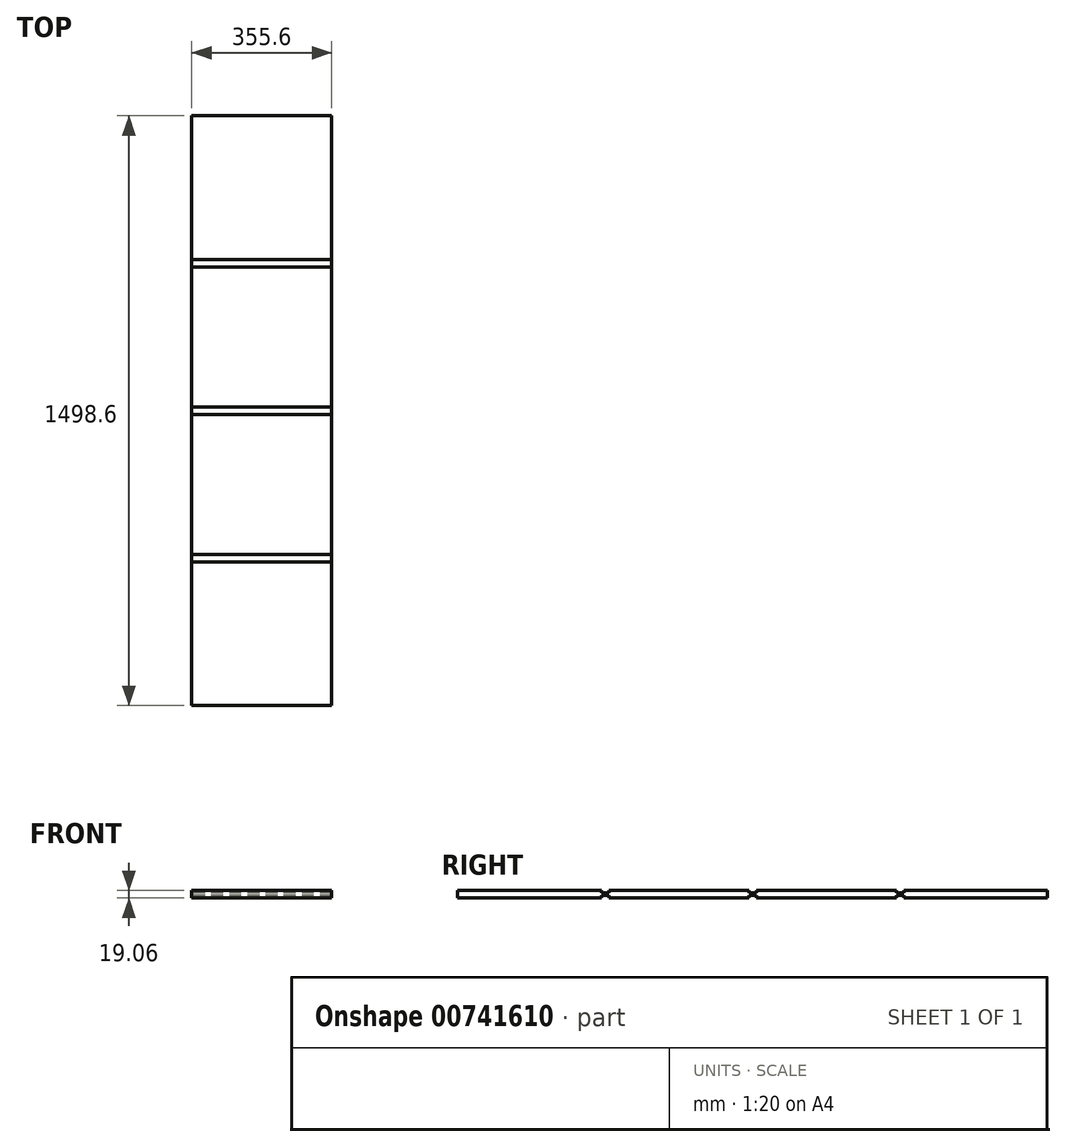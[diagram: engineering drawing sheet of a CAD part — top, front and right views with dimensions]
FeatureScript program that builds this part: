
annotation { "Feature Type Name" : "Feature", "Feature Type Description" : "" }
export const myFeature = defineFeature(function(context is Context, id is Id, definition is map)
    precondition{}
    {
        {
            var Q0;
            Q0=qCreatedBy(makeId("Right.planeOp"),FACE);
            var sketch = newSketch(context, id + "F0", { "sketchPlane" : qUnion([Q0])});
            skLineSegment(sketch, "E0.bottom", {"start": v(749.3, 9.53) * mm, "end": v(384.17, 9.53) * mm});
            skLineSegment(sketch, "E0.top", {"start": v(749.3, -9.53) * mm, "end": v(384.17, -9.53) * mm});
            skLineSegment(sketch, "E0.left", {"start": v(749.3, 9.52) * mm, "end": v(749.3, -9.52) * mm});
            skLineSegment(sketch, "E0.right", {"start": v(-749.3, 9.53) * mm, "end": v(-749.3, -9.53) * mm});
            skPoint(sketch, "E0.middle", {"position": v(0, 0) * mm});
            skLineSegment(sketch, "E1", {"start": v(-749.3, 9.53) * mm, "end": v(-384.17, 9.53) * mm});
            skLineSegment(sketch, "E2.top", {"start": v(-384.17, 3.18) * mm, "end": v(-365.12, 3.18) * mm});
            skLineSegment(sketch, "E2.left", {"start": v(-384.17, 9.53) * mm, "end": v(-384.17, 3.18) * mm});
            skLineSegment(sketch, "E2.right", {"start": v(-365.12, 9.53) * mm, "end": v(-365.12, 3.18) * mm});
            skLineSegment(sketch, "E3", {"start": v(-365.12, 9.53) * mm, "end": v(-9.52, 9.53) * mm});
            skLineSegment(sketch, "E4.top", {"start": v(-9.52, 3.18) * mm, "end": v(0, 3.18) * mm});
            skLineSegment(sketch, "E4.left", {"start": v(-9.52, 9.53) * mm, "end": v(-9.52, 3.18) * mm});
            skLineSegment(sketch, "E5.MirrorCS", {"start": v(9.52, 3.18) * mm, "end": v(0, 3.18) * mm});
            skLineSegment(sketch, "E6.MirrorCS", {"start": v(9.52, 9.53) * mm, "end": v(9.52, 3.18) * mm});
            skLineSegment(sketch, "E7.MirrorCS", {"start": v(365.12, 9.53) * mm, "end": v(365.12, 3.18) * mm});
            skLineSegment(sketch, "E8.MirrorCS", {"start": v(384.17, 3.18) * mm, "end": v(365.12, 3.18) * mm});
            skLineSegment(sketch, "E9.MirrorCS", {"start": v(384.17, 9.53) * mm, "end": v(384.17, 3.18) * mm});
            skLineSegment(sketch, "E10.MirrorCS", {"start": v(-384.17, -9.53) * mm, "end": v(-384.17, -3.18) * mm});
            skLineSegment(sketch, "E11.MirrorCS", {"start": v(-384.17, -3.18) * mm, "end": v(-365.12, -3.18) * mm});
            skLineSegment(sketch, "E12.MirrorCS", {"start": v(-365.12, -9.53) * mm, "end": v(-365.12, -3.18) * mm});
            skLineSegment(sketch, "E13.MirrorCS", {"start": v(-9.52, -9.53) * mm, "end": v(-9.52, -3.18) * mm});
            skLineSegment(sketch, "E14.MirrorCS", {"start": v(-9.52, -3.18) * mm, "end": v(0, -3.18) * mm});
            skLineSegment(sketch, "E15.MirrorCS", {"start": v(9.52, -3.18) * mm, "end": v(0, -3.18) * mm});
            skLineSegment(sketch, "E16.MirrorCS", {"start": v(9.52, -9.53) * mm, "end": v(9.52, -3.18) * mm});
            skLineSegment(sketch, "E17.MirrorCS", {"start": v(365.12, -9.53) * mm, "end": v(365.12, -3.18) * mm});
            skLineSegment(sketch, "E18.MirrorCS", {"start": v(384.17, -3.18) * mm, "end": v(365.12, -3.18) * mm});
            skLineSegment(sketch, "E19.MirrorCS", {"start": v(384.17, -9.53) * mm, "end": v(384.17, -3.18) * mm});
            skLineSegment(sketch, "E20.trimOffspring", {"start": v(-384.17, 9.53) * mm, "end": v(-749.3, 9.53) * mm});
            skLineSegment(sketch, "E21.trimOffspring", {"start": v(-384.17, -9.53) * mm, "end": v(-749.3, -9.53) * mm});
            skLineSegment(sketch, "E22.trimOffspring", {"start": v(-9.52, -9.53) * mm, "end": v(-365.12, -9.53) * mm});
            skLineSegment(sketch, "E23.trimOffspring", {"start": v(-9.52, 9.53) * mm, "end": v(-365.12, 9.53) * mm});
            skLineSegment(sketch, "E24.trimOffspring", {"start": v(365.12, -9.53) * mm, "end": v(9.52, -9.53) * mm});
            skLineSegment(sketch, "E25.trimOffspring", {"start": v(365.12, 9.53) * mm, "end": v(9.52, 9.53) * mm});
            skSolve(sketch);
        }
        {
            var Q0;
            Q0 = qSketchRegion(id + "F0", true);
            extrude(context, id + "F1", {"entities" : qUnion([Q0]), "depth" : 355.6 * mm, "offsetDistance" : 25.4 * mm});
        }
    });
